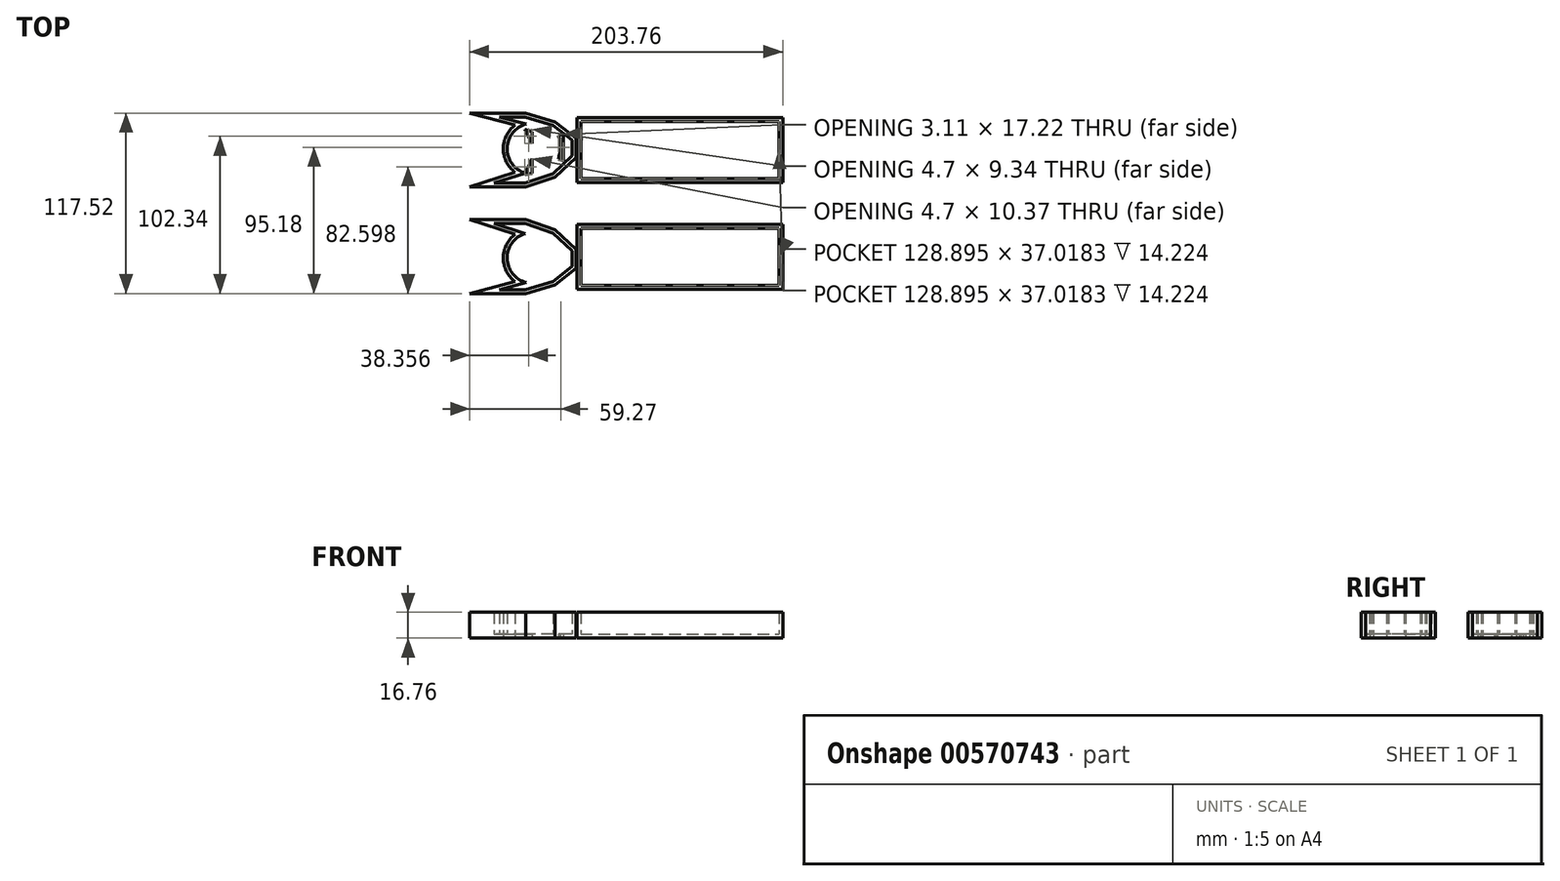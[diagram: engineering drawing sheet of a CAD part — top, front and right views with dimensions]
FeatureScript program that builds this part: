
annotation { "Feature Type Name" : "Feature", "Feature Type Description" : "" }
export const myFeature = defineFeature(function(context is Context, id is Id, definition is map)
    precondition{}
    {
        {
            var Q0;
            Q0=qCreatedBy(makeId("Top.planeOp"),FACE);
            var sketch = newSketch(context, id + "F0", { "sketchPlane" : qUnion([Q0])});
            skLineSegment(sketch, "E0.bottom", {"start": v(-62.34, 13.72) * mm, "end": v(71.64, 13.72) * mm});
            skLineSegment(sketch, "E0.top", {"start": v(-62.34, 55.82) * mm, "end": v(71.64, 55.82) * mm});
            skLineSegment(sketch, "E0.left", {"start": v(-62.34, 13.72) * mm, "end": v(-62.34, 55.82) * mm});
            skLineSegment(sketch, "E0.right", {"start": v(71.64, 13.72) * mm, "end": v(71.64, 55.82) * mm});
            skLineSegment(sketch, "E1.MirrorCS", {"start": v(-62.34, -13.72) * mm, "end": v(71.64, -13.72) * mm});
            skLineSegment(sketch, "E2.MirrorCS", {"start": v(-62.34, -13.72) * mm, "end": v(-62.34, -55.82) * mm});
            skLineSegment(sketch, "E3.MirrorCS", {"start": v(-62.34, -55.82) * mm, "end": v(71.64, -55.82) * mm});
            skLineSegment(sketch, "E4.MirrorCS", {"start": v(71.64, -13.72) * mm, "end": v(71.64, -55.82) * mm});
            skLineSegment(sketch, "E5", {"start": v(-63.01, 29.85) * mm, "end": v(-63.01, 42.35) * mm});
            skLineSegment(sketch, "E6", {"start": v(-63.01, 42.35) * mm, "end": v(-76.57, 53.06) * mm});
            skLineSegment(sketch, "E7", {"start": v(-63.01, 29.85) * mm, "end": v(-76.57, 17.12) * mm});
            skLineSegment(sketch, "E8", {"start": v(-76.57, 17.12) * mm, "end": v(-95.53, 10.61) * mm});
            skLineSegment(sketch, "E9", {"start": v(-76.57, 53.06) * mm, "end": v(-95.53, 58.76) * mm});
            skLineSegment(sketch, "E10", {"start": v(-95.53, 10.61) * mm, "end": v(-132.12, 10.61) * mm});
            skLineSegment(sketch, "E11", {"start": v(-132.12, 10.61) * mm, "end": v(-102.59, 20.22) * mm});
            skLineSegment(sketch, "E12", {"start": v(-95.53, 58.76) * mm, "end": v(-132.12, 58.76) * mm});
            skLineSegment(sketch, "E13", {"start": v(-132.12, 58.76) * mm, "end": v(-102.59, 50.92) * mm});
            skArc(sketch, "E14", {"start": v(-102.59, 50.92) * mm, "mid": v(-110.26, 35.57) * mm, "end": v(-102.59, 20.22) * mm});
            skLineSegment(sketch, "E15.MirrorCS", {"start": v(-76.57, -17.12) * mm, "end": v(-95.53, -10.61) * mm});
            skLineSegment(sketch, "E16.MirrorCS", {"start": v(-63.01, -29.85) * mm, "end": v(-76.57, -17.12) * mm});
            skLineSegment(sketch, "E17.MirrorCS", {"start": v(-63.01, -29.85) * mm, "end": v(-63.01, -42.35) * mm});
            skLineSegment(sketch, "E18.MirrorCS", {"start": v(-63.01, -42.35) * mm, "end": v(-76.57, -53.06) * mm});
            skLineSegment(sketch, "E19.MirrorCS", {"start": v(-76.57, -53.06) * mm, "end": v(-95.53, -58.76) * mm});
            skLineSegment(sketch, "E20.MirrorCS", {"start": v(-95.53, -58.76) * mm, "end": v(-132.12, -58.76) * mm});
            skLineSegment(sketch, "E21.MirrorCS", {"start": v(-132.12, -58.76) * mm, "end": v(-102.59, -50.92) * mm});
            skArc(sketch, "E22.MirrorCS", {"start": v(-102.59, -50.92) * mm, "mid": v(-110.26, -35.57) * mm, "end": v(-102.59, -20.22) * mm});
            skLineSegment(sketch, "E23.MirrorCS", {"start": v(-132.12, -10.61) * mm, "end": v(-102.59, -20.22) * mm});
            skLineSegment(sketch, "E24.MirrorCS", {"start": v(-95.53, -10.61) * mm, "end": v(-132.12, -10.61) * mm});
            skSolve(sketch);
        }
        {
            var Q0;
            Q0 = qSketchRegion(id + "F0", true);
            extrude(context, id + "F1", {"entities" : qUnion([Q0]), "depth" : 16.76 * mm, "offsetDistance" : 25.4 * mm});
        }
        {
            var Q0;
            Q0=makeQuery(id+"F1.opExtrude","CAP_FACE",FACE,{"disambiguationData":[OSD([sQuery(id+"F0.wireOp",EDGE,"E0.bottom"),sQuery(id+"F0.wireOp",EDGE,"E0.top"),sQuery(id+"F0.wireOp",EDGE,"E0.left"),sQuery(id+"F0.wireOp",EDGE,"E0.right")])],"isStart":false});
            var Q1;
            Q1=makeQuery(id+"F1.opExtrude","CAP_FACE",FACE,{"disambiguationData":[OSD([sQuery(id+"F0.wireOp",EDGE,"E1.MirrorCS"),sQuery(id+"F0.wireOp",EDGE,"E2.MirrorCS"),sQuery(id+"F0.wireOp",EDGE,"E3.MirrorCS"),sQuery(id+"F0.wireOp",EDGE,"E4.MirrorCS")])],"isStart":false});
            shell(context, id + "F2", {"entities" : qUnion([Q0, Q1]), "thickness" : 2.54 * mm});
        }
        {
            var Q0;
            Q0=qCreatedBy(makeId("Top.planeOp"),FACE);
            var sketch = newSketch(context, id + "F3", { "sketchPlane" : qUnion([Q0])});
            skArc(sketch, "E25", {"start": v(-74.4, 28.7) * mm, "mid": v(-73.24, 36.35) * mm, "end": v(-74.34, 44) * mm});
            skLineSegment(sketch, "E26", {"start": v(-74.4, 28.7) * mm, "end": v(-71.3, 27.81) * mm});
            skLineSegment(sketch, "E27", {"start": v(-74.34, 44) * mm, "end": v(-71.3, 45.03) * mm});
            skLineSegment(sketch, "E28", {"start": v(-71.3, 45.03) * mm, "end": v(-71.3, 27.81) * mm});
            skSolve(sketch);
        }
        {
            var Q0;
            Q0=qCreatedBy(makeId("Top.planeOp"),FACE);
            var sketch = newSketch(context, id + "F4", { "sketchPlane" : qUnion([Q0])});
            skLineSegment(sketch, "E29", {"start": v(-91.41, 46.66) * mm, "end": v(-91.41, 38.91) * mm});
            skLineSegment(sketch, "E30", {"start": v(-91.41, 29.02) * mm, "end": v(-91.41, 19.76) * mm});
            skLineSegment(sketch, "E31", {"start": v(-91.41, 38.91) * mm, "end": v(-96.12, 48.25) * mm});
            skLineSegment(sketch, "E32", {"start": v(-91.41, 29.02) * mm, "end": v(-96.12, 18.65) * mm});
            skLineSegment(sketch, "E33", {"start": v(-96.12, 18.65) * mm, "end": v(-91.41, 19.76) * mm});
            skLineSegment(sketch, "E34", {"start": v(-96.12, 48.25) * mm, "end": v(-91.41, 46.66) * mm});
            skSolve(sketch);
        }
        {
            var Q0;
            Q0=makeQuery(id+"F1.opExtrude","CAP_FACE",FACE,{"disambiguationData":[OSD([sQuery(id+"F0.wireOp",EDGE,"E5"),sQuery(id+"F0.wireOp",EDGE,"E6"),sQuery(id+"F0.wireOp",EDGE,"E7"),sQuery(id+"F0.wireOp",EDGE,"E8"),sQuery(id+"F0.wireOp",EDGE,"E9"),sQuery(id+"F0.wireOp",EDGE,"E10"),sQuery(id+"F0.wireOp",EDGE,"E11"),sQuery(id+"F0.wireOp",EDGE,"E12"),sQuery(id+"F0.wireOp",EDGE,"E13"),sQuery(id+"F0.wireOp",EDGE,"E14")])],"isStart":false});
            shell(context, id + "F5", {"entities" : qUnion([Q0]), "thickness" : 2.54 * mm});
        }
        {
            var Q0;
            Q0=makeQuery(id+"F1.opExtrude","CAP_FACE",FACE,{"disambiguationData":[OSD([sQuery(id+"F0.wireOp",EDGE,"E15.MirrorCS"),sQuery(id+"F0.wireOp",EDGE,"E16.MirrorCS"),sQuery(id+"F0.wireOp",EDGE,"E17.MirrorCS"),sQuery(id+"F0.wireOp",EDGE,"E18.MirrorCS"),sQuery(id+"F0.wireOp",EDGE,"E19.MirrorCS"),sQuery(id+"F0.wireOp",EDGE,"E20.MirrorCS"),sQuery(id+"F0.wireOp",EDGE,"E21.MirrorCS"),sQuery(id+"F0.wireOp",EDGE,"E22.MirrorCS"),sQuery(id+"F0.wireOp",EDGE,"E23.MirrorCS"),sQuery(id+"F0.wireOp",EDGE,"E24.MirrorCS")])],"isStart":false});
            shell(context, id + "F6", {"entities" : qUnion([Q0]), "thickness" : 2.54 * mm});
        }
        {
            var Q0;
            Q0 = qSketchRegion(id + "F4", true);
            extrude(context, id + "F7", {"entities" : qUnion([Q0]), "operationType" : NewBodyOperationType.REMOVE, "depth" : 39.37 * mm, "offsetDistance" : 25.4 * mm});
        }
        {
            var Q0;
            Q0 = qSketchRegion(id + "F3", true);
            extrude(context, id + "F8", {"entities" : qUnion([Q0]), "operationType" : NewBodyOperationType.REMOVE, "depth" : 66.55 * mm, "offsetDistance" : 25.4 * mm});
        }
    });
